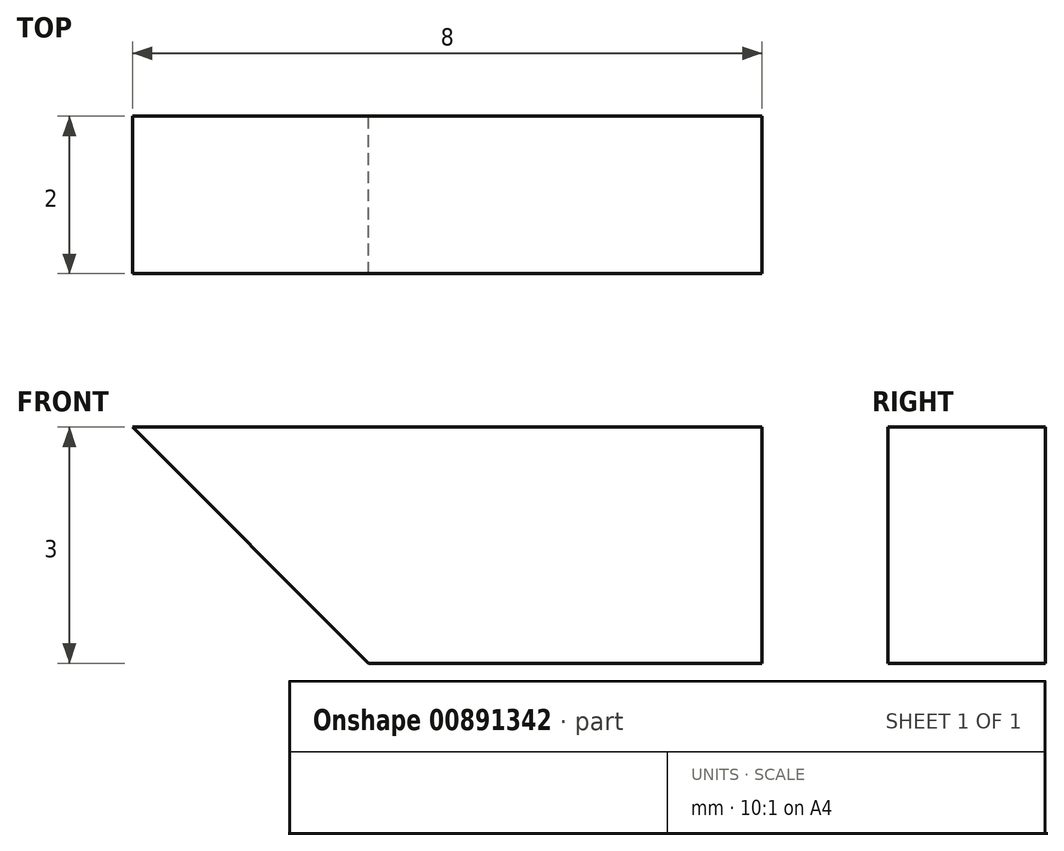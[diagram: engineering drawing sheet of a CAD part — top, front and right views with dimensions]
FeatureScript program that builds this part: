
annotation { "Feature Type Name" : "Feature", "Feature Type Description" : "" }
export const myFeature = defineFeature(function(context is Context, id is Id, definition is map)
    precondition{}
    {
        {
            var Q0;
            Q0=qCreatedBy(makeId("Top.planeOp"),FACE);
            var sketch = newSketch(context, id + "F0", { "sketchPlane" : qUnion([Q0])});
            skLineSegment(sketch, "E0.bottom", {"start": v(-4, 1) * mm, "end": v(4, 1) * mm});
            skLineSegment(sketch, "E0.top", {"start": v(-4, -1) * mm, "end": v(4, -1) * mm});
            skLineSegment(sketch, "E0.left", {"start": v(-4, 1) * mm, "end": v(-4, -1) * mm});
            skLineSegment(sketch, "E0.right", {"start": v(4, 1) * mm, "end": v(4, -1) * mm});
            skPoint(sketch, "E0.middle", {"position": v(0, 0) * mm});
            skSolve(sketch);
        }
        {
            var Q0;
            Q0=makeQuery(id+"F0.imprint","IMPRINT",FACE,{"disambiguationData":[TD([[makeQuery(id+"F0.imprint","IMPRINT",EDGE,{"derivedFrom":sQuery(id+"F0.wireOp",EDGE,"E0.bottom")}),-1.0]])]});
            extrude(context, id + "F1", {"entities" : qUnion([Q0]), "depth" : 3 * mm, "offsetDistance" : 25 * mm});
        }
        {
            var Q0;
            Q0=makeQuery(id+"F1.opExtrude","CAP_EDGE",EDGE,{"disambiguationData":[OSD([sQuery(id+"F0.wireOp",EDGE,"E0.left")])],"isStart":true});
            chamfer(context, id + "F2", {"entities" : qUnion([Q0]), "width" : 3 * mm, "tangentPropagation" : true});
        }
    });
